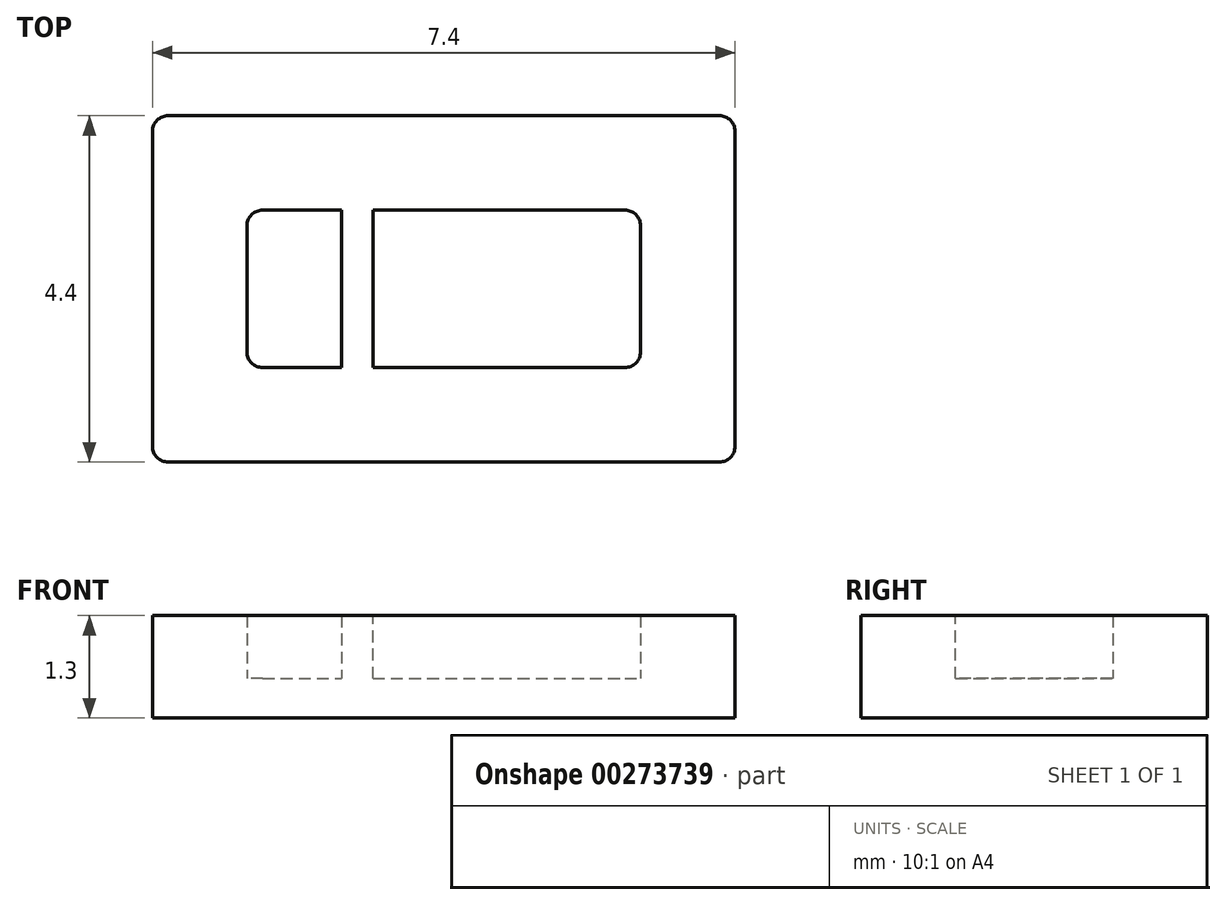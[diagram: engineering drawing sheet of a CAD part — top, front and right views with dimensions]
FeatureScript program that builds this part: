
annotation { "Feature Type Name" : "Feature", "Feature Type Description" : "" }
export const myFeature = defineFeature(function(context is Context, id is Id, definition is map)
    precondition{}
    {
        {
            var Q0;
            Q0=qCreatedBy(makeId("Top.planeOp"),FACE);
            var sketch = newSketch(context, id + "F0", { "sketchPlane" : qUnion([Q0])});
            skLineSegment(sketch, "E0.bottom", {"start": v(-5, 0) * mm, "end": v(0, 0) * mm});
            skLineSegment(sketch, "E0.top", {"start": v(-5, -2) * mm, "end": v(0, -2) * mm});
            skLineSegment(sketch, "E0.left", {"start": v(0, 0) * mm, "end": v(0, -2) * mm});
            skLineSegment(sketch, "E0.right", {"start": v(-5, 0) * mm, "end": v(-5, -2) * mm});
            skLineSegment(sketch, "E1.0", {"start": v(-6.2, 1.2) * mm, "end": v(1.2, 1.2) * mm});
            skLineSegment(sketch, "E1.1", {"start": v(-6.2, 1.2) * mm, "end": v(-6.2, -3.2) * mm});
            skLineSegment(sketch, "E1.2", {"start": v(-6.2, -3.2) * mm, "end": v(1.2, -3.2) * mm});
            skLineSegment(sketch, "E1.3", {"start": v(1.2, 1.2) * mm, "end": v(1.2, -3.2) * mm});
            skSolve(sketch);
        }
        {
            var Q0;
            {var subQ1=sQuery(id+"F0.wireOp",EDGE,"E0.left");Q0=makeQuery(id+"F0.imprint","IMPRINT",FACE,{"disambiguationData":[TD([[makeQuery(id+"F0.imprint","IMPRINT",EDGE,{"derivedFrom":subQ1}),1.0]])]});}
            var Q1;
            {var subQ0=sQuery(id+"F0.wireOp",EDGE,"PltnrTD2-t7eW-fMYP-iMQx-yhnUqNyawp66");Q1=makeQuery(id+"F0.imprint","IMPRINT",FACE,{"disambiguationData":[TD([[makeQuery(id+"F0.imprint","IMPRINT",EDGE,{"derivedFrom":subQ0}),1.0]])]});}
            var Q2;
            {var subQ0=sQuery(id+"F0.wireOp",EDGE,"GaU8u7SS-o1hA-pSsI-QdnM-VgOe5ZE7k3Az");Q2=makeQuery(id+"F0.imprint","IMPRINT",FACE,{"disambiguationData":[TD([[makeQuery(id+"F0.imprint","IMPRINT",EDGE,{"derivedFrom":subQ0}),-1.0]])]});}
            extrude(context, id + "F1", {"entities" : qUnion([Q0, Q1, Q2]), "depth" : 0.8 * mm, "offsetDistance" : 25 * mm});
        }
        {
            var Q0;
            {var subQ1=sQuery(id+"F0.wireOp",EDGE,"E0.left");Q0=makeQuery(id+"F0.imprint","IMPRINT",FACE,{"disambiguationData":[TD([[makeQuery(id+"F0.imprint","IMPRINT",EDGE,{"derivedFrom":subQ1}),1.0]])]});}
            var Q1;
            {var subQ3=sQuery(id+"F0.wireOp",EDGE,"E0.left");Q1=makeQuery(id+"F0.imprint","IMPRINT",FACE,{"disambiguationData":[TD([[makeQuery(id+"F0.imprint","IMPRINT",EDGE,{"derivedFrom":subQ3}),-1.0]])]});}
            var Q2;
            {var subQ0=sQuery(id+"F0.wireOp",EDGE,"PltnrTD2-t7eW-fMYP-iMQx-yhnUqNyawp66");Q2=makeQuery(id+"F0.imprint","IMPRINT",FACE,{"disambiguationData":[TD([[makeQuery(id+"F0.imprint","IMPRINT",EDGE,{"derivedFrom":subQ0}),1.0]])]});}
            var Q3;
            {var subQ0=sQuery(id+"F0.wireOp",EDGE,"GaU8u7SS-o1hA-pSsI-QdnM-VgOe5ZE7k3Az");Q3=makeQuery(id+"F0.imprint","IMPRINT",FACE,{"disambiguationData":[TD([[makeQuery(id+"F0.imprint","IMPRINT",EDGE,{"derivedFrom":subQ0}),-1.0]])]});}
            extrude(context, id + "F2", {"entities" : qUnion([Q0, Q1, Q2, Q3]), "operationType" : NewBodyOperationType.ADD, "oppositeDirection" : true, "depth" : 0.5 * mm, "offsetDistance" : 25 * mm});
        }
        {
            var Q0;
            Q0=qCreatedBy(makeId("Top.planeOp"),FACE);
            var sketch = newSketch(context, id + "F3", { "sketchPlane" : qUnion([Q0])});
            skLineSegment(sketch, "E2.0", {"start": v(-18.2, 13.2) * mm, "end": v(13.2, 13.2) * mm});
            skLineSegment(sketch, "E2.1", {"start": v(-18.2, 13.2) * mm, "end": v(-18.2, -15.2) * mm});
            skLineSegment(sketch, "E2.2", {"start": v(-18.2, -15.2) * mm, "end": v(13.2, -15.2) * mm});
            skLineSegment(sketch, "E2.3", {"start": v(13.2, 13.2) * mm, "end": v(13.2, -15.2) * mm});
            skSolve(sketch);
        }
        {
            var Q0;
            Q0=makeQuery(id+"F1.opExtrude","SWEPT_EDGE",EDGE,{"disambiguationData":[OSD([sQuery(id+"F0.wireOp",EDGE,"E0.bottom"),sQuery(id+"F0.wireOp",EDGE,"E0.right")])]});
            var Q1;
            Q1=makeQuery(id+"F1.opExtrude","SWEPT_EDGE",EDGE,{"disambiguationData":[OSD([sQuery(id+"F0.wireOp",EDGE,"E0.bottom"),sQuery(id+"F0.wireOp",EDGE,"E0.left")])]});
            var Q2;
            Q2=makeQuery(id+"F1.opExtrude","SWEPT_EDGE",EDGE,{"disambiguationData":[OSD([sQuery(id+"F0.wireOp",EDGE,"E0.top"),sQuery(id+"F0.wireOp",EDGE,"E0.left")])]});
            var Q3;
            Q3=makeQuery(id+"F1.opExtrude","SWEPT_EDGE",EDGE,{"disambiguationData":[OSD([sQuery(id+"F0.wireOp",EDGE,"E0.top"),sQuery(id+"F0.wireOp",EDGE,"E0.right")])]});
            var Q4;
            Q4=makeQuery(id+"F1.opExtrude","SWEPT_EDGE",EDGE,{"disambiguationData":[OSD([sQuery(id+"F0.wireOp",EDGE,"E0.top"),sQuery(id+"F0.wireOp",EDGE,"GaU8u7SS-o1hA-pSsI-QdnM-VgOe5ZE7k3Az")])]});
            var Q5;
            Q5=makeQuery(id+"F1.opExtrude","SWEPT_EDGE",EDGE,{"disambiguationData":[OSD([sQuery(id+"F0.wireOp",EDGE,"E0.top"),sQuery(id+"F0.wireOp",EDGE,"6Q4BuRyY-vjzR-DwkS-BJ9a-7LxTlb2drnym")])]});
            var Q6;
            Q6=makeQuery(id+"F1.opExtrude","SWEPT_EDGE",EDGE,{"disambiguationData":[OSD([sQuery(id+"F0.wireOp",EDGE,"E0.bottom"),sQuery(id+"F0.wireOp",EDGE,"IQAd5D1V-hCRT-c3wt-y3hK-GECXJAOESLXm")])]});
            var Q7;
            Q7=makeQuery(id+"F1.opExtrude","SWEPT_EDGE",EDGE,{"disambiguationData":[OSD([sQuery(id+"F0.wireOp",EDGE,"E0.bottom"),sQuery(id+"F0.wireOp",EDGE,"PltnrTD2-t7eW-fMYP-iMQx-yhnUqNyawp66")])]});
            var Q8;
            {var subQ0=sQuery(id+"F0.wireOp",EDGE,"E1.1");var subQ1=sQuery(id+"F0.wireOp",EDGE,"E1.0");Q8=makeQuery(id+"F2.boolean.opBoolean","MERGE",EDGE,{"derivedFrom":[makeQuery(id+"F1.opExtrude","SWEPT_EDGE",EDGE,{"disambiguationData":[OSD([subQ1,subQ0])]}),makeQuery(id+"F2.opExtrude","SWEPT_EDGE",EDGE,{"disambiguationData":[OSD([subQ1,subQ0])]})]});}
            var Q9;
            {var subQ0=sQuery(id+"F0.wireOp",EDGE,"E1.3");var subQ1=sQuery(id+"F0.wireOp",EDGE,"E1.0");Q9=makeQuery(id+"F2.boolean.opBoolean","MERGE",EDGE,{"derivedFrom":[makeQuery(id+"F1.opExtrude","SWEPT_EDGE",EDGE,{"disambiguationData":[OSD([subQ1,subQ0])]}),makeQuery(id+"F2.opExtrude","SWEPT_EDGE",EDGE,{"disambiguationData":[OSD([subQ1,subQ0])]})]});}
            var Q10;
            {var subQ0=sQuery(id+"F0.wireOp",EDGE,"E1.3");var subQ1=sQuery(id+"F0.wireOp",EDGE,"E1.2");Q10=makeQuery(id+"F2.boolean.opBoolean","MERGE",EDGE,{"derivedFrom":[makeQuery(id+"F1.opExtrude","SWEPT_EDGE",EDGE,{"disambiguationData":[OSD([subQ1,subQ0])]}),makeQuery(id+"F2.opExtrude","SWEPT_EDGE",EDGE,{"disambiguationData":[OSD([subQ1,subQ0])]})]});}
            var Q11;
            {var subQ0=sQuery(id+"F0.wireOp",EDGE,"E1.2");var subQ1=sQuery(id+"F0.wireOp",EDGE,"E1.1");Q11=makeQuery(id+"F2.boolean.opBoolean","MERGE",EDGE,{"derivedFrom":[makeQuery(id+"F1.opExtrude","SWEPT_EDGE",EDGE,{"disambiguationData":[OSD([subQ1,subQ0])]}),makeQuery(id+"F2.opExtrude","SWEPT_EDGE",EDGE,{"disambiguationData":[OSD([subQ1,subQ0])]})]});}
            fillet(context, id + "F4", {"entities" : qUnion([Q0, Q1, Q2, Q3, Q4, Q5, Q6, Q7, Q8, Q9, Q10, Q11]), "radius" : 0.2 * mm, "tangentPropagation" : true, "allowEdgeOverflow" : false});
        }
        {
            var Q0;
            Q0=makeQuery(id+"F1.opExtrude","SWEPT_FACE",FACE,{"disambiguationData":[OSD([sQuery(id+"F0.wireOp",EDGE,"E0.bottom")])]});
            var sketch = newSketch(context, id + "F5", { "sketchPlane" : qUnion([Q0])});
            skLineSegment(sketch, "E3.bottom", {"start": v(-3.8, 0.8) * mm, "end": v(-3.4, 0.8) * mm});
            skLineSegment(sketch, "E3.top", {"start": v(-3.8, 0) * mm, "end": v(-3.4, 0) * mm});
            skLineSegment(sketch, "E3.left", {"start": v(-3.8, 0.8) * mm, "end": v(-3.8, 0) * mm});
            skLineSegment(sketch, "E3.right", {"start": v(-3.4, 0.8) * mm, "end": v(-3.4, 0) * mm});
            skLineSegment(sketch, "E4", {"start": v(-3.8, 0.8) * mm, "end": v(-4.8, 0.8) * mm, "construction": true});
            skSolve(sketch);
        }
        {
            var Q0;
            Q0=makeQuery(id+"F5.imprint","IMPRINT",FACE,{"disambiguationData":[TD([[makeQuery(id+"F5.imprint","IMPRINT",EDGE,{"derivedFrom":sQuery(id+"F5.wireOp",EDGE,"E3.bottom")}),-1.0]])]});
            extrude(context, id + "F6", {"entities" : qUnion([Q0]), "operationType" : NewBodyOperationType.ADD, "endBound" : BoundingType.UP_TO_NEXT, "depth" : 25 * mm, "offsetDistance" : 25 * mm});
        }
    });
